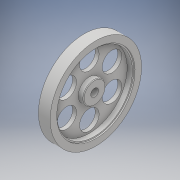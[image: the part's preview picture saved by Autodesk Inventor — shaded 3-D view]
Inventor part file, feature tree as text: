
AUTODESK INVENTOR PART (.ipt)
format: ipt  version: 2018 (Build 220112000, 112)  size: 175,104 bytes
history: native  units: mm
features: sketch x7, extrude x6, hole x1, fillet x1, projected_geometry x1
ambient origin geometry x8: Origin, YZ Plane, XZ Plane, XY Plane, X Axis, Y Axis, Z Axis, Center Point
bodies: Solid1 (feature_tree)
feature tree (16):
  extrude  "Extrusion1"  Depth=9.0mm TaperAngle=0.0deg
  extrude  "Extrusion2"  Depth=5.0mm
  extrude  "Extrusion3"  Depth=1.0mm TaperAngle=0.0deg
  extrude  "Extrusion4"  Depth=4.0mm TaperAngle=0.0deg
  extrude  "Extrusion5"  Depth=4.0mm TaperAngle=0.0deg
  extrude  "Extrusion6"  Depth=1.0mm
  hole  "Hole1"  [1 undecoded]
  fillet  "Fillet1"  Radius=60.0mm
  sketch  "Sketch1"  dims[d0=70.0mm d1=9.0mm d2=0.0mm]
  sketch  "Sketch2"  dims[d3=6.0mm d4=5.0mm]
  sketch  "Sketch3"  dims[d5=0.0mm d6=1.0mm d7=0.0mm]
  projected_geometry  "Projected Loop1"
  sketch  "Sketch4"  dims[d8=17.0mm d9=4.0mm d10=0.0mm]
  sketch  "Sketch5"  dims[d11=6.0mm d12=4.0mm d13=0.0mm]
  sketch  "Sketch6"  dims[d14=1.0mm d15=1.0mm]
  sketch  "Sketch7"  dims[d16=1.0mm d17=0.0mm d18=20.0mm d19=60.0mm d21=360.0deg d23=15.0mm d24=6.0mm d25=4.0mm d26=2.0mm d27=90.0deg d28=8.0mm d29=0.0mm d30=0.5mm]
note: 1 required parameter value undecoded (feature->parameter linkage not recoverable at this tier; creation-order binding heuristic only, values carry confidence <= 0.55)
